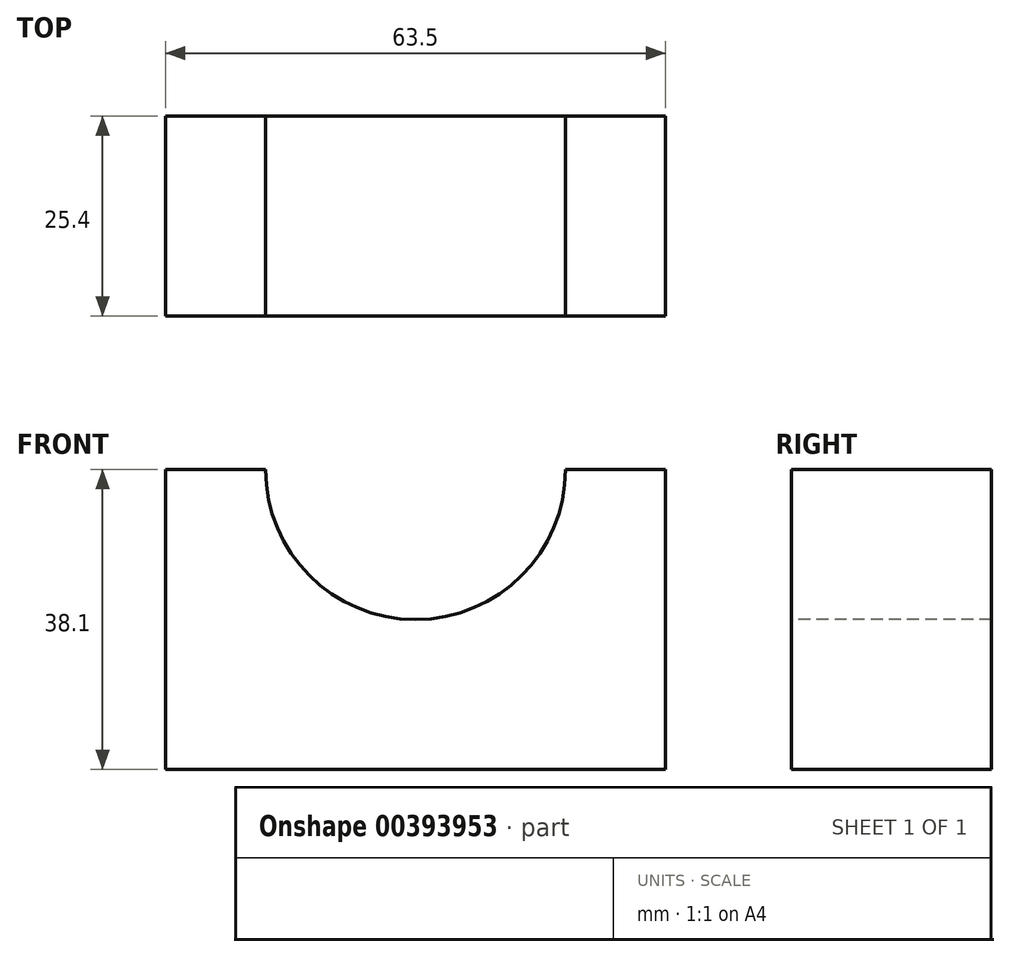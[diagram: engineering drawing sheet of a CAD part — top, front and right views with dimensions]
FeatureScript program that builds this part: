
annotation { "Feature Type Name" : "Feature", "Feature Type Description" : "" }
export const myFeature = defineFeature(function(context is Context, id is Id, definition is map)
    precondition{}
    {
        {
            var Q0;
            Q0=qCreatedBy(makeId("Front.planeOp"),FACE);
            var sketch = newSketch(context, id + "F0", { "sketchPlane" : qUnion([Q0])});
            skLineSegment(sketch, "E0", {"start": v(0, 0) * mm, "end": v(0, 38.1) * mm});
            skLineSegment(sketch, "E1", {"start": v(0, 38.1) * mm, "end": v(63.5, 38.1) * mm});
            skLineSegment(sketch, "E2", {"start": v(63.5, 38.1) * mm, "end": v(63.5, 0) * mm});
            skLineSegment(sketch, "E3", {"start": v(63.5, 0) * mm, "end": v(0, 0) * mm});
            skSolve(sketch);
        }
        {
            var Q0;
            Q0=qSketchRegion(id+"F0",true);
            extrude(context, id + "F1", {"entities" : qUnion([Q0]), "depth" : 25.4 * mm});
        }
        {
            var Q0;
            Q0=makeQuery(id+"F1.opExtrude","CAP_FACE",FACE,{"disambiguationData":[OSD([sQuery(id+"F0.wireOp",EDGE,"E0"),sQuery(id+"F0.wireOp",EDGE,"E1"),sQuery(id+"F0.wireOp",EDGE,"E2"),sQuery(id+"F0.wireOp",EDGE,"E3")])],"isStart":false});
            var sketch = newSketch(context, id + "F2", { "sketchPlane" : qUnion([Q0])});
            skCircle(sketch, "E4", {"center": v(31.75, 38.1) * mm, "radius": 19.05 * mm});
            skSolve(sketch);
        }
        {
            var Q0;
            Q0=qSketchRegion(id+"F2",true);
            extrude(context, id + "F3", {"entities" : qUnion([Q0]), "operationType" : NewBodyOperationType.REMOVE, "oppositeDirection" : true, "depth" : 25.4 * mm});
        }
    });
